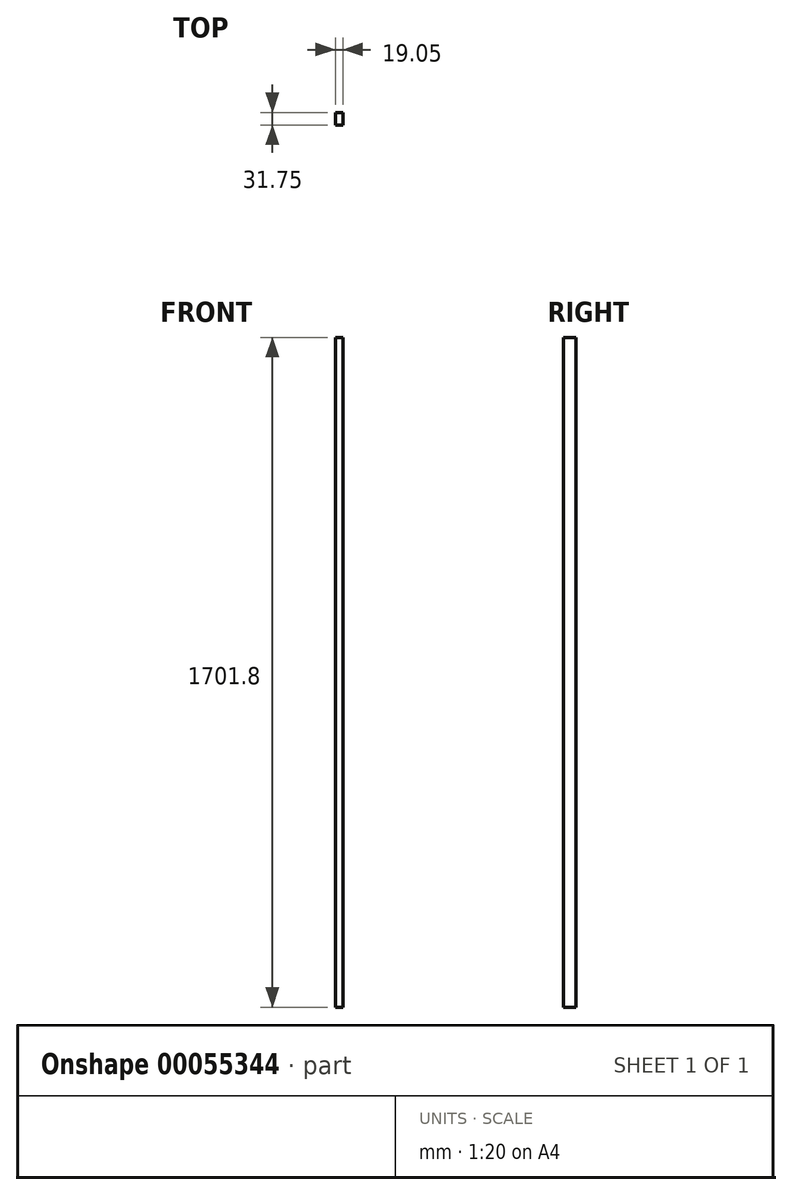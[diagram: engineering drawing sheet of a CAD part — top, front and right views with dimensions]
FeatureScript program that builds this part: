
annotation { "Feature Type Name" : "Feature", "Feature Type Description" : "" }
export const myFeature = defineFeature(function(context is Context, id is Id, definition is map)
    precondition{}
    {
        {
            var Q0;
            Q0=qCreatedBy(makeId("Front.planeOp"),FACE);
            var sketch = newSketch(context, id + "F0", { "sketchPlane" : qUnion([Q0])});
            skLineSegment(sketch, "E0.bottom", {"start": v(0, 0) * mm, "end": v(19.05, 0) * mm});
            skLineSegment(sketch, "E0.top", {"start": v(0, 1701.8) * mm, "end": v(19.05, 1701.8) * mm});
            skLineSegment(sketch, "E0.left", {"start": v(0, 0) * mm, "end": v(0, 1701.8) * mm});
            skLineSegment(sketch, "E0.right", {"start": v(19.05, 0) * mm, "end": v(19.05, 1701.8) * mm});
            skSolve(sketch);
        }
        {
            var Q0;
            Q0 = qSketchRegion(id + "F0", true);
            extrude(context, id + "F1", {"entities" : qUnion([Q0]), "oppositeDirection" : true, "depth" : 31.75 * mm});
        }
    });
